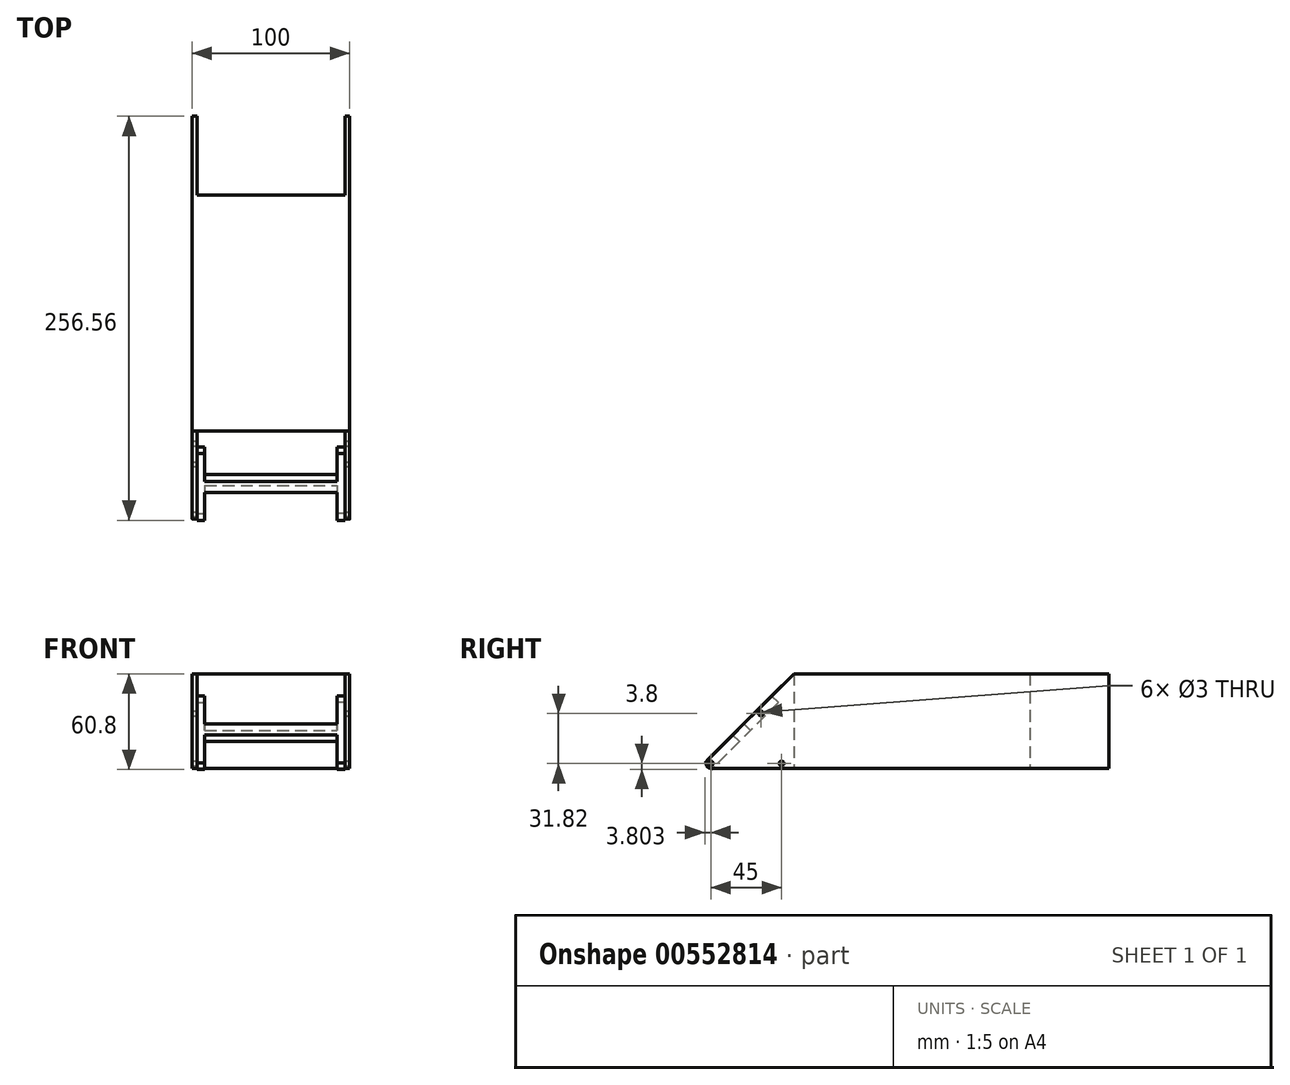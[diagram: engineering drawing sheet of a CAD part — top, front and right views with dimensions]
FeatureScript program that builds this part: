
annotation { "Feature Type Name" : "Feature", "Feature Type Description" : "" }
export const myFeature = defineFeature(function(context is Context, id is Id, definition is map)
    precondition{}
    {
        {
            var Q0;
            Q0=qCreatedBy(makeId("Front.planeOp"),FACE);
            var sketch = newSketch(context, id + "F0", { "sketchPlane" : qUnion([Q0])});
            skLineSegment(sketch, "E0.bottom", {"start": v(50, 30) * mm, "end": v(-50, 30) * mm});
            skLineSegment(sketch, "E0.top", {"start": v(50, -30) * mm, "end": v(-50, -30) * mm});
            skLineSegment(sketch, "E0.left", {"start": v(50, 30) * mm, "end": v(50, -30) * mm});
            skLineSegment(sketch, "E0.right", {"start": v(-50, 30) * mm, "end": v(-50, -30) * mm});
            skPoint(sketch, "E0.middle", {"position": v(0, 0) * mm});
            skSolve(sketch);
        }
        {
            var Q0;
            Q0 = qSketchRegion(id + "F0", true);
            extrude(context, id + "F1", {"entities" : qUnion([Q0]), "endBound" : BoundingType.SYMMETRIC, "depth" : 150 * mm, "offsetDistance" : 25.4 * mm});
        }
        {
            var Q0;
            Q0=makeQuery(id+"F1.opExtrude","SWEPT_FACE",FACE,{"disambiguationData":[OSD([sQuery(id+"F0.wireOp",EDGE,"E0.left")])]});
            var sketch = newSketch(context, id + "F2", { "sketchPlane" : qUnion([Q0])});
            skLineSegment(sketch, "E1.0", {"start": v(-75, 30) * mm, "end": v(-75, -30) * mm});
            skLineSegment(sketch, "E2", {"start": v(-75, 30) * mm, "end": v(-129.88, -24.88) * mm});
            skLineSegment(sketch, "E3", {"start": v(-75, -30) * mm, "end": v(-127.76, -30) * mm});
            skPoint(sketch, "E4.orphan", {"position": v(-135, -30) * mm});
            skArc(sketch, "E5.filletArc", {"start": v(-129.88, -24.88) * mm, "mid": v(-130.53, -28.15) * mm, "end": v(-127.76, -30) * mm});
            skLineSegment(sketch, "E6", {"start": v(-127.76, -27) * mm, "end": v(-75, -27) * mm, "construction": true});
            skLineSegment(sketch, "E7", {"start": v(-75, -27) * mm, "end": v(-127.76, -27) * mm, "construction": true});
            skLineSegment(sketch, "E8", {"start": v(-127.76, -27) * mm, "end": v(-75, 25.76) * mm, "construction": true});
            skPoint(sketch, "E9", {"position": v(-82.76, -27) * mm});
            skPoint(sketch, "E10", {"position": v(-95.94, 4.82) * mm});
            skSolve(sketch);
        }
        {
            var Q0;
            Q0=makeQuery(id+"F2.imprint","IMPRINT",FACE,{"disambiguationData":[TD([[makeQuery(id+"F2.imprint","IMPRINT",EDGE,{"derivedFrom":sQuery(id+"F2.wireOp",EDGE,"E1.0")}),-1.0]])]});
            extrude(context, id + "F3", {"entities" : qUnion([Q0]), "operationType" : NewBodyOperationType.ADD, "oppositeDirection" : true, "depth" : 3 * mm, "offsetDistance" : 25 * mm});
        }
        {
            var Q0;
            Q0=makeQuery(id+"F1.opExtrude","SWEPT_BODY",BODY,{"disambiguationData":[OSD([sQuery(id+"F0.wireOp",EDGE,"E0.bottom"),sQuery(id+"F0.wireOp",EDGE,"E0.top"),sQuery(id+"F0.wireOp",EDGE,"E0.left"),sQuery(id+"F0.wireOp",EDGE,"E0.right")])]});
            var Q1;
            Q1=qCreatedBy(makeId("Right.planeOp"),FACE);
            mirror(context, id + "F4", {"operationType" : NewBodyOperationType.ADD, "entities" : qUnion([Q0]), "mirrorPlane" : qUnion([Q1])});
        }
        {
            var Q0;
            Q0=sQuery(id+"F2.wireOp",VERTEX,"E10");
            var Q1;
            Q1=sQuery(id+"F2.wireOp",VERTEX,"E6.start");
            var Q2;
            Q2=sQuery(id+"F2.wireOp",VERTEX,"E9");
            var Q3;
            Q3=makeQuery(id+"F1.opExtrude","SWEPT_BODY",BODY,{"disambiguationData":[OSD([sQuery(id+"F0.wireOp",EDGE,"E0.bottom"),sQuery(id+"F0.wireOp",EDGE,"E0.top"),sQuery(id+"F0.wireOp",EDGE,"E0.left"),sQuery(id+"F0.wireOp",EDGE,"E0.right")])]});
            hole(context, id + "F5", {"style" : HoleStyle.SIMPLE, "endStyle" : HoleEndStyle.THROUGH, "holeDiameter" : 3 * mm, "majorDiameter" : 5 * mm, "isTappedThrough" : true, "tappedDepth" : 12 * mm, "tapClearance" : 3, "locations" : qUnion([Q0, Q1, Q2]), "scope" : qUnion([Q3])});
        }
        {
            var Q0;
            Q0=makeQuery(id+"F4.opPattern","COPY",FACE,{"derivedFrom":makeQuery(id+"F3.opExtrude","SWEPT_FACE",FACE,{"disambiguationData":[OSD([sQuery(id+"F2.wireOp",EDGE,"E2")])]}),"instanceName":"1"});
            var sketch = newSketch(context, id + "F6", { "sketchPlane" : qUnion([Q0])});
            skLineSegment(sketch, "E11.bottom", {"start": v(-47, -51.8) * mm, "end": v(-42, -51.8) * mm});
            skLineSegment(sketch, "E11.top", {"start": v(-47, -111.8) * mm, "end": v(-42, -111.8) * mm});
            skLineSegment(sketch, "E11.left", {"start": v(-47, -51.8) * mm, "end": v(-47, -111.8) * mm});
            skLineSegment(sketch, "E11.right", {"start": v(-42, -51.8) * mm, "end": v(-42, -111.8) * mm});
            skLineSegment(sketch, "E12.bottom", {"start": v(47, -51.8) * mm, "end": v(42, -51.8) * mm});
            skLineSegment(sketch, "E12.top", {"start": v(47, -111.8) * mm, "end": v(42, -111.8) * mm});
            skLineSegment(sketch, "E12.left", {"start": v(47, -51.8) * mm, "end": v(47, -111.8) * mm});
            skLineSegment(sketch, "E12.right", {"start": v(42, -51.8) * mm, "end": v(42, -111.8) * mm});
            skLineSegment(sketch, "E13", {"start": v(-42, -81.8) * mm, "end": v(42, -81.8) * mm, "construction": true});
            skLineSegment(sketch, "E14.0", {"start": v(-42, -86.8) * mm, "end": v(42, -86.8) * mm});
            skLineSegment(sketch, "E15.0", {"start": v(-42, -76.8) * mm, "end": v(42, -76.8) * mm});
            skSolve(sketch);
        }
        {
            var Q0;
            Q0 = qSketchRegion(id + "F6", true);
            extrude(context, id + "F7", {"entities" : qUnion([Q0]), "oppositeDirection" : true, "depth" : 6 * mm, "offsetDistance" : 25 * mm});
        }
        {
            var Q0;
            Q0=makeQuery(id+"F2.imprint","IMPRINT",FACE,{"disambiguationData":[TD([[makeQuery(id+"F2.imprint","IMPRINT",EDGE,{"derivedFrom":sQuery(id+"F2.wireOp",EDGE,"E1.0")}),1.0]])]});
            var sketch = newSketch(context, id + "F8", { "sketchPlane" : qUnion([Q0])});
            skLineSegment(sketch, "E16.0", {"start": v(75, 30) * mm, "end": v(75, -30) * mm});
            skLineSegment(sketch, "E17.bottom", {"start": v(75, 30) * mm, "end": v(125, 30) * mm});
            skLineSegment(sketch, "E17.top", {"start": v(75, -30) * mm, "end": v(125, -30) * mm});
            skLineSegment(sketch, "E17.right", {"start": v(125, 30) * mm, "end": v(125, -30) * mm});
            skSolve(sketch);
        }
        {
            var Q0;
            Q0=makeQuery(id+"F8.imprint","IMPRINT",FACE,{"disambiguationData":[TD([[makeQuery(id+"F8.imprint","IMPRINT",EDGE,{"derivedFrom":sQuery(id+"F8.wireOp",EDGE,"E17.bottom")}),-1.0]])]});
            extrude(context, id + "F9", {"entities" : qUnion([Q0]), "oppositeDirection" : true, "depth" : 3 * mm, "offsetDistance" : 25 * mm});
        }
        {
            var Q0;
            Q0=makeQuery(id+"F9.opExtrude","SWEPT_BODY",BODY,{"disambiguationData":[OSD([sQuery(id+"F8.wireOp",EDGE,"E17.bottom"),sQuery(id+"F8.wireOp",EDGE,"E17.top"),sQuery(id+"F8.wireOp",EDGE,"E16.0"),sQuery(id+"F8.wireOp",EDGE,"E17.right")])]});
            var Q1;
            Q1=qCreatedBy(makeId("Right.planeOp"),FACE);
            mirror(context, id + "F10", {"operationType" : NewBodyOperationType.ADD, "entities" : qUnion([Q0]), "mirrorPlane" : qUnion([Q1])});
        }
    });
